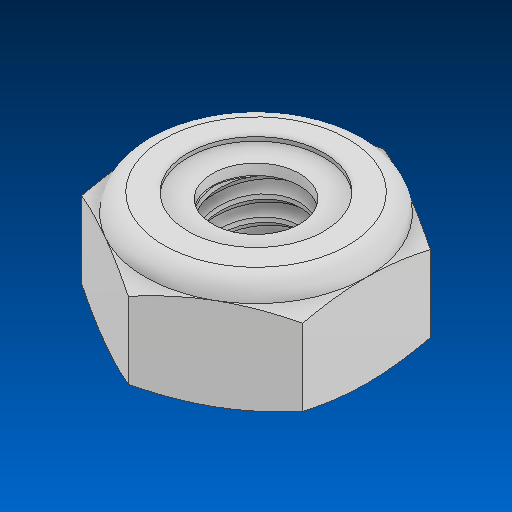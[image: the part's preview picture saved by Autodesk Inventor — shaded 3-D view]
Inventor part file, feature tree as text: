
AUTODESK INVENTOR PART (.ipt)
format: ipt  version: 2022.2 (Build 262287000, 287)  size: 287,744 bytes
history: native  units: in
note: dims shown in document units (in); Inventor stores cm internally (conversion verified against a paired STEP export)
features: other x1, revolve x1
ambient origin geometry x8: Origin, YZ Plane, XZ Plane, XY Plane, X Axis, Y Axis, Z Axis, Center Point
bodies: Solid1 (feature_tree), Solid2 (feature_tree)
feature tree (2):
  other  "Cut-Revolve4"
  revolve  "Revolve2"  [1 undecoded]
note: 1 required parameter value undecoded (feature->parameter linkage not recoverable at this tier; creation-order binding heuristic only, values carry confidence <= 0.55)
